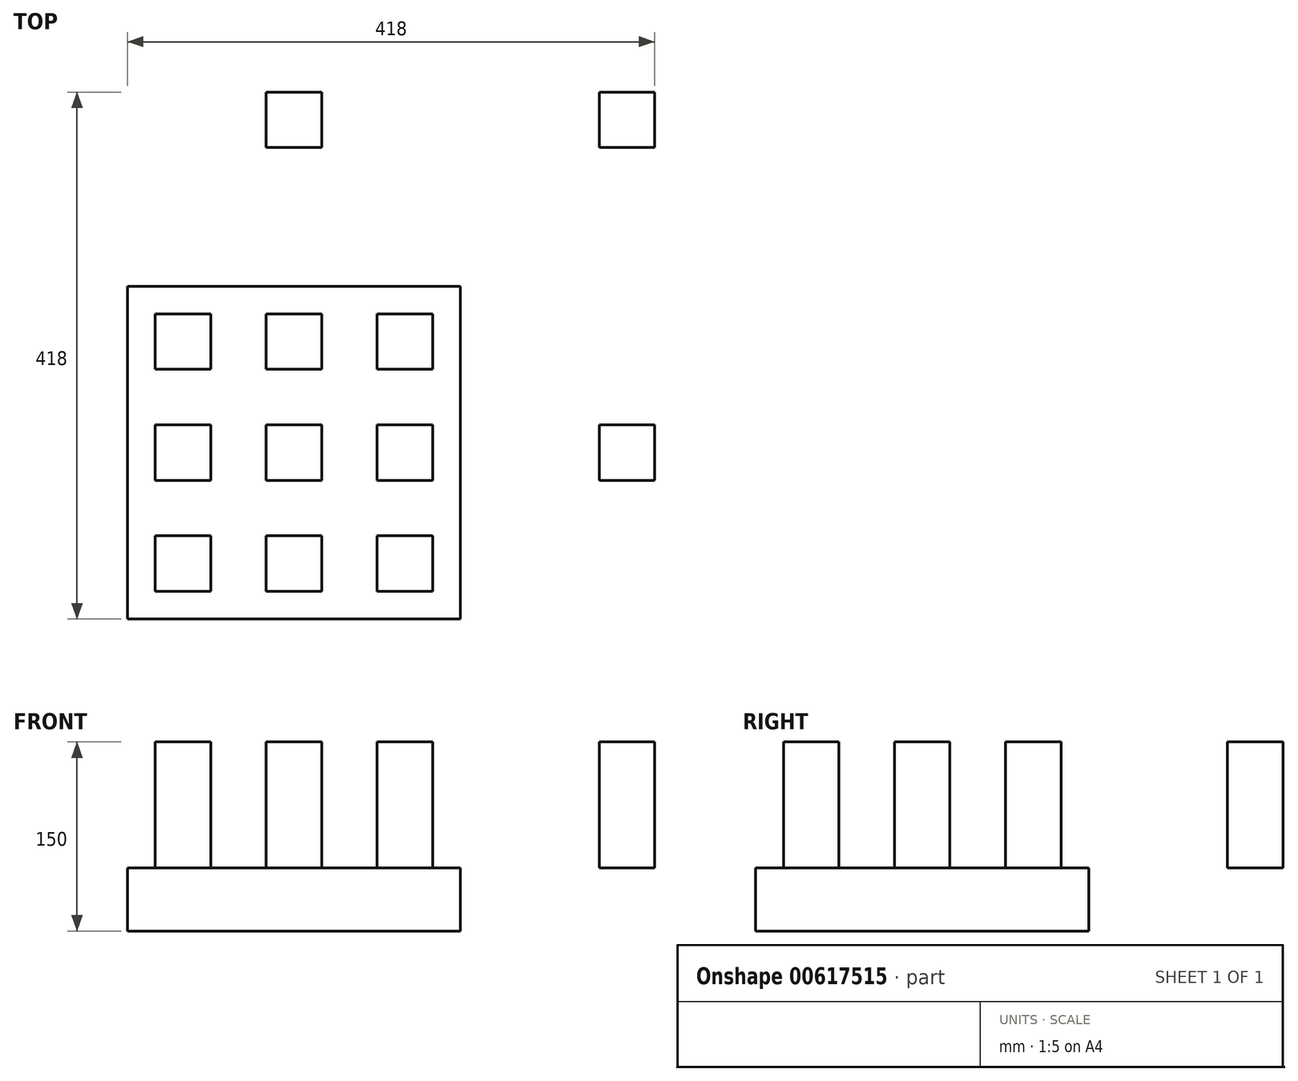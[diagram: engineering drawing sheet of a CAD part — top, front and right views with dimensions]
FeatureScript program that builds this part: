
annotation { "Feature Type Name" : "Feature", "Feature Type Description" : "" }
export const myFeature = defineFeature(function(context is Context, id is Id, definition is map)
    precondition{}
    {
        {
            var Q0;
            Q0=qCreatedBy(makeId("Top.planeOp"),FACE);
            var sketch = newSketch(context, id + "F0", { "sketchPlane" : qUnion([Q0])});
            skLineSegment(sketch, "E0.bottom", {"start": v(22, -22) * mm, "end": v(-22, -22) * mm});
            skLineSegment(sketch, "E0.top", {"start": v(22, 22) * mm, "end": v(-22, 22) * mm});
            skLineSegment(sketch, "E0.left", {"start": v(22, -22) * mm, "end": v(22, 22) * mm});
            skLineSegment(sketch, "E0.right", {"start": v(-22, -22) * mm, "end": v(-22, 22) * mm});
            skPoint(sketch, "E0.middle", {"position": v(0, 0) * mm});
            skLineSegment(sketch, "E1.bottom", {"start": v(-66, -22) * mm, "end": v(-110, -22) * mm});
            skLineSegment(sketch, "E1.top", {"start": v(-66, 22) * mm, "end": v(-110, 22) * mm});
            skLineSegment(sketch, "E1.left", {"start": v(-66, -22) * mm, "end": v(-66, 22) * mm});
            skLineSegment(sketch, "E1.right", {"start": v(-110, -22) * mm, "end": v(-110, 22) * mm});
            skPoint(sketch, "E1.middle", {"position": v(-88, 0) * mm});
            skPoint(sketch, "E1.middle.positionSnap0", {"position": v(-22, 0) * mm});
            skPoint(sketch, "E1.centerSnap0", {"position": v(-22, 0) * mm});
            skLineSegment(sketch, "E2.bottom", {"start": v(22, 66) * mm, "end": v(-22, 66) * mm});
            skLineSegment(sketch, "E2.top", {"start": v(22, 110) * mm, "end": v(-22, 110) * mm});
            skLineSegment(sketch, "E2.left", {"start": v(22, 66) * mm, "end": v(22, 110) * mm});
            skLineSegment(sketch, "E2.right", {"start": v(-22, 66) * mm, "end": v(-22, 110) * mm});
            skLineSegment(sketch, "E3.bottom", {"start": v(-66, 66) * mm, "end": v(-110, 66) * mm});
            skLineSegment(sketch, "E3.top", {"start": v(-66, 110) * mm, "end": v(-110, 110) * mm});
            skLineSegment(sketch, "E3.left", {"start": v(-66, 66) * mm, "end": v(-66, 110) * mm});
            skLineSegment(sketch, "E3.right", {"start": v(-110, 66) * mm, "end": v(-110, 110) * mm});
            skLineSegment(sketch, "E4.bottom", {"start": v(-132, 132) * mm, "end": v(132, 132) * mm});
            skLineSegment(sketch, "E4.top", {"start": v(-132, -132) * mm, "end": v(132, -132) * mm});
            skLineSegment(sketch, "E4.left", {"start": v(-132, 132) * mm, "end": v(-132, -132) * mm});
            skLineSegment(sketch, "E4.right", {"start": v(132, 132) * mm, "end": v(132, -132) * mm});
            skSolve(sketch);
        }
        {
            var Q0;
            Q0=makeQuery(id+"F0.imprint","IMPRINT",FACE,{"disambiguationData":[TD([[makeQuery(id+"F0.imprint","IMPRINT",EDGE,{"derivedFrom":sQuery(id+"F0.wireOp",EDGE,"E1.bottom")}),-1.0]])]});
            var Q1;
            Q1=makeQuery(id+"F0.imprint","IMPRINT",FACE,{"disambiguationData":[TD([[makeQuery(id+"F0.imprint","IMPRINT",EDGE,{"derivedFrom":sQuery(id+"F0.wireOp",EDGE,"E3.bottom")}),-1.0]])]});
            var Q2;
            Q2=makeQuery(id+"F0.imprint","IMPRINT",FACE,{"disambiguationData":[TD([[makeQuery(id+"F0.imprint","IMPRINT",EDGE,{"derivedFrom":sQuery(id+"F0.wireOp",EDGE,"E2.bottom")}),-1.0]])]});
            var Q3;
            Q3=makeQuery(id+"F0.imprint","IMPRINT",FACE,{"disambiguationData":[TD([[makeQuery(id+"F0.imprint","IMPRINT",EDGE,{"derivedFrom":sQuery(id+"F0.wireOp",EDGE,"E0.bottom")}),-1.0]])]});
            extrude(context, id + "F1", {"entities" : qUnion([Q0, Q1, Q2, Q3]), "depth" : 100 * mm, "offsetDistance" : 25 * mm});
        }
        {
            var Q0;
            Q0=makeQuery(id+"F1.opExtrude","SWEPT_BODY",BODY,{"disambiguationData":[OSD([sQuery(id+"F0.wireOp",EDGE,"E1.bottom"),sQuery(id+"F0.wireOp",EDGE,"E1.top"),sQuery(id+"F0.wireOp",EDGE,"E1.left"),sQuery(id+"F0.wireOp",EDGE,"E1.right")])]});
            var Q1;
            Q1=makeQuery(id+"F1.opExtrude","SWEPT_BODY",BODY,{"disambiguationData":[OSD([sQuery(id+"F0.wireOp",EDGE,"E3.bottom"),sQuery(id+"F0.wireOp",EDGE,"E3.top"),sQuery(id+"F0.wireOp",EDGE,"E3.left"),sQuery(id+"F0.wireOp",EDGE,"E3.right")])]});
            var Q2;
            Q2=qCreatedBy(makeId("Right.planeOp"),FACE);
            mirror(context, id + "F2", {"entities" : qUnion([Q0, Q1]), "mirrorPlane" : qUnion([Q2])});
        }
        {
            var Q0;
            Q0=makeQuery(id+"F1.opExtrude","SWEPT_BODY",BODY,{"disambiguationData":[OSD([sQuery(id+"F0.wireOp",EDGE,"E3.bottom"),sQuery(id+"F0.wireOp",EDGE,"E3.top"),sQuery(id+"F0.wireOp",EDGE,"E3.left"),sQuery(id+"F0.wireOp",EDGE,"E3.right")])]});
            var Q1;
            Q1=makeQuery(id+"F1.opExtrude","SWEPT_BODY",BODY,{"disambiguationData":[OSD([sQuery(id+"F0.wireOp",EDGE,"E2.bottom"),sQuery(id+"F0.wireOp",EDGE,"E2.top"),sQuery(id+"F0.wireOp",EDGE,"E2.left"),sQuery(id+"F0.wireOp",EDGE,"E2.right")])]});
            var Q2;
            Q2=makeQuery(id+"F2.opPattern","COPY",BODY,{"derivedFrom":makeQuery(id+"F1.opExtrude","SWEPT_BODY",BODY,{"disambiguationData":[OSD([sQuery(id+"F0.wireOp",EDGE,"E3.bottom"),sQuery(id+"F0.wireOp",EDGE,"E3.top"),sQuery(id+"F0.wireOp",EDGE,"E3.left"),sQuery(id+"F0.wireOp",EDGE,"E3.right")])]}),"instanceName":"1"});
            var Q3;
            Q3=qCreatedBy(makeId("Front.planeOp"),FACE);
            mirror(context, id + "F3", {"entities" : qUnion([Q0, Q1, Q2]), "mirrorPlane" : qUnion([Q3])});
        }
        {
            var Q0;
            Q0=makeQuery(id+"F0.imprint","IMPRINT",FACE,{"disambiguationData":[TD([[makeQuery(id+"F0.imprint","IMPRINT",EDGE,{"derivedFrom":sQuery(id+"F0.wireOp",EDGE,"E0.bottom")}),1.0]])]});
            var Q1;
            Q1=makeQuery(id+"F0.imprint","IMPRINT",FACE,{"disambiguationData":[TD([[makeQuery(id+"F0.imprint","IMPRINT",EDGE,{"derivedFrom":sQuery(id+"F0.wireOp",EDGE,"E1.bottom")}),-1.0]])]});
            var Q2;
            Q2=makeQuery(id+"F0.imprint","IMPRINT",FACE,{"disambiguationData":[TD([[makeQuery(id+"F0.imprint","IMPRINT",EDGE,{"derivedFrom":sQuery(id+"F0.wireOp",EDGE,"E0.bottom")}),-1.0]])]});
            var Q3;
            Q3=makeQuery(id+"F0.imprint","IMPRINT",FACE,{"disambiguationData":[TD([[makeQuery(id+"F0.imprint","IMPRINT",EDGE,{"derivedFrom":sQuery(id+"F0.wireOp",EDGE,"E3.bottom")}),-1.0]])]});
            var Q4;
            Q4=makeQuery(id+"F0.imprint","IMPRINT",FACE,{"disambiguationData":[TD([[makeQuery(id+"F0.imprint","IMPRINT",EDGE,{"derivedFrom":sQuery(id+"F0.wireOp",EDGE,"E2.bottom")}),-1.0]])]});
            extrude(context, id + "F4", {"entities" : qUnion([Q0, Q1, Q2, Q3, Q4]), "oppositeDirection" : true, "depth" : 50 * mm, "offsetDistance" : 25 * mm});
        }
        {
            var Q0;
            Q0=makeQuery(id+"F1.opExtrude","SWEPT_BODY",BODY,{"disambiguationData":[OSD([sQuery(id+"F0.wireOp",EDGE,"E0.bottom"),sQuery(id+"F0.wireOp",EDGE,"E0.top"),sQuery(id+"F0.wireOp",EDGE,"E0.left"),sQuery(id+"F0.wireOp",EDGE,"E0.right")])]});
            transform(context, id + "F5", {"entities" : qUnion([Q0]), "transformType" : TransformType.TRANSLATION_3D, "dx" : 264 * mm, "dy" : 0 * mm, "dz" : 0 * mm, "makeCopy" : true});
        }
        {
            var Q0;
            Q0=makeQuery(id+"F5.opPattern","COPY",BODY,{"derivedFrom":makeQuery(id+"F1.opExtrude","SWEPT_BODY",BODY,{"disambiguationData":[OSD([sQuery(id+"F0.wireOp",EDGE,"E0.bottom"),sQuery(id+"F0.wireOp",EDGE,"E0.top"),sQuery(id+"F0.wireOp",EDGE,"E0.left"),sQuery(id+"F0.wireOp",EDGE,"E0.right")])]}),"instanceName":"1"});
            transform(context, id + "F6", {"entities" : qUnion([Q0]), "transformType" : TransformType.TRANSLATION_3D, "dx" : 0 * mm, "dy" : 264 * mm, "dz" : 0 * mm, "makeCopy" : true});
        }
        {
            var Q0;
            Q0=makeQuery(id+"F1.opExtrude","SWEPT_BODY",BODY,{"disambiguationData":[OSD([sQuery(id+"F0.wireOp",EDGE,"E0.bottom"),sQuery(id+"F0.wireOp",EDGE,"E0.top"),sQuery(id+"F0.wireOp",EDGE,"E0.left"),sQuery(id+"F0.wireOp",EDGE,"E0.right")])]});
            transform(context, id + "F7", {"entities" : qUnion([Q0]), "transformType" : TransformType.TRANSLATION_3D, "dx" : 0 * mm, "dy" : 264 * mm, "dz" : 0 * mm, "makeCopy" : true});
        }
    });
